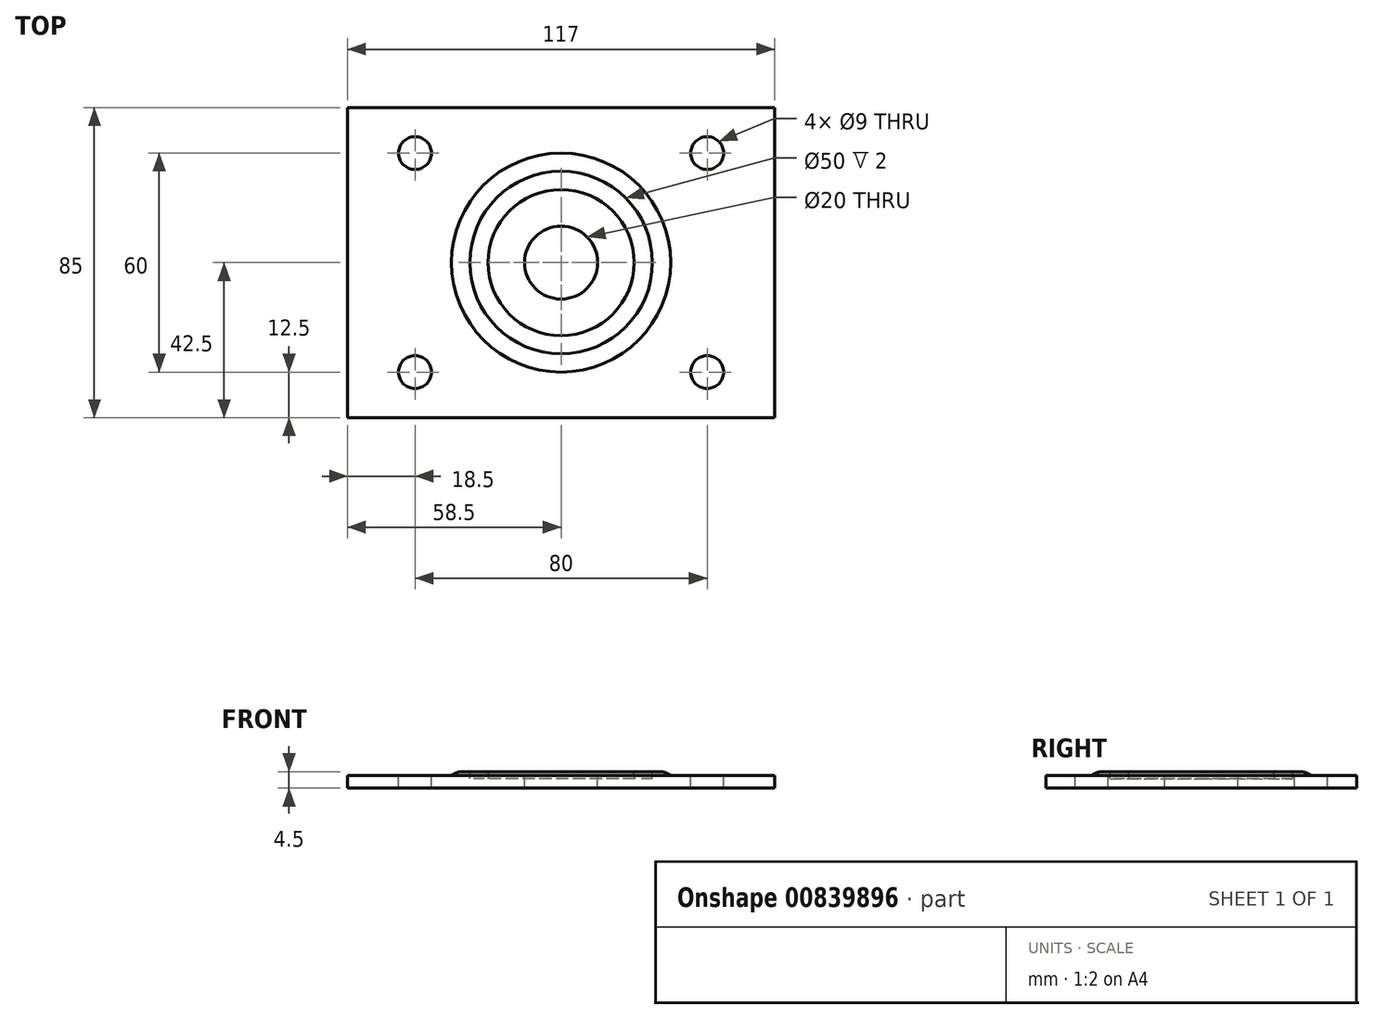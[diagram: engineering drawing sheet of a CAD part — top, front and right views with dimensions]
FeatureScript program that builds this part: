
annotation { "Feature Type Name" : "Feature", "Feature Type Description" : "" }
export const myFeature = defineFeature(function(context is Context, id is Id, definition is map)
    precondition{}
    {
        {
            var Q0;
            Q0=qCreatedBy(makeId("Top.planeOp"),FACE);
            var sketch = newSketch(context, id + "F0", { "sketchPlane" : qUnion([Q0])});
            skLineSegment(sketch, "E0.bottom", {"start": v(58.5, -42.5) * mm, "end": v(-58.5, -42.5) * mm});
            skLineSegment(sketch, "E0.top", {"start": v(58.5, 42.5) * mm, "end": v(-58.5, 42.5) * mm});
            skLineSegment(sketch, "E0.left", {"start": v(58.5, -42.5) * mm, "end": v(58.5, 42.5) * mm});
            skLineSegment(sketch, "E0.right", {"start": v(-58.5, -42.5) * mm, "end": v(-58.5, 42.5) * mm});
            skPoint(sketch, "E0.middle", {"position": v(0, 0) * mm});
            skSolve(sketch);
        }
        {
            var Q0;
            Q0 = qSketchRegion(id + "F0", true);
            extrude(context, id + "F1", {"entities" : qUnion([Q0]), "depth" : 3.5 * mm, "offsetDistance" : 25 * mm});
        }
        {
            var Q0;
            Q0=makeQuery(id+"F1.opExtrude","CAP_FACE",FACE,{"disambiguationData":[OSD([sQuery(id+"F0.wireOp",EDGE,"E0.bottom"),sQuery(id+"F0.wireOp",EDGE,"E0.top"),sQuery(id+"F0.wireOp",EDGE,"E0.left"),sQuery(id+"F0.wireOp",EDGE,"E0.right")])],"isStart":false});
            var sketch = newSketch(context, id + "F2", { "sketchPlane" : qUnion([Q0])});
            skLineSegment(sketch, "E1.bottom", {"start": v(40, -30) * mm, "end": v(-40, -30) * mm, "construction": true});
            skLineSegment(sketch, "E1.top", {"start": v(40, 30) * mm, "end": v(-40, 30) * mm, "construction": true});
            skLineSegment(sketch, "E1.left", {"start": v(40, -30) * mm, "end": v(40, 30) * mm, "construction": true});
            skLineSegment(sketch, "E1.right", {"start": v(-40, -30) * mm, "end": v(-40, 30) * mm, "construction": true});
            skPoint(sketch, "E1.middle", {"position": v(0, 0) * mm});
            skCircle(sketch, "E2", {"center": v(40, 30) * mm, "radius": 4.5 * mm});
            skCircle(sketch, "E3", {"center": v(-40, 30) * mm, "radius": 4.5 * mm});
            skCircle(sketch, "E4", {"center": v(-40, -30) * mm, "radius": 4.5 * mm});
            skCircle(sketch, "E5", {"center": v(40, -30) * mm, "radius": 4.5 * mm});
            skSolve(sketch);
        }
        {
            var Q0;
            Q0 = qSketchRegion(id + "F2", true);
            extrude(context, id + "F3", {"entities" : qUnion([Q0]), "operationType" : NewBodyOperationType.REMOVE, "oppositeDirection" : true, "depth" : 25 * mm, "offsetDistance" : 25 * mm});
        }
        {
            var Q0;
            Q0=makeQuery(id+"F1.opExtrude","CAP_FACE",FACE,{"disambiguationData":[OSD([sQuery(id+"F0.wireOp",EDGE,"E0.bottom"),sQuery(id+"F0.wireOp",EDGE,"E0.top"),sQuery(id+"F0.wireOp",EDGE,"E0.left"),sQuery(id+"F0.wireOp",EDGE,"E0.right")])],"isStart":false});
            var sketch = newSketch(context, id + "F4", { "sketchPlane" : qUnion([Q0])});
            skCircle(sketch, "E6", {"center": v(0, 0) * mm, "radius": 30 * mm});
            skSolve(sketch);
        }
        {
            var Q0;
            Q0 = qSketchRegion(id + "F4", true);
            extrude(context, id + "F5", {"entities" : qUnion([Q0]), "operationType" : NewBodyOperationType.ADD, "depth" : 1 * mm, "offsetDistance" : 25 * mm});
        }
        {
            var Q0;
            Q0=makeQuery(id+"F5.opExtrude","CAP_EDGE",EDGE,{"disambiguationData":[OSD([sQuery(id+"F4.wireOp",EDGE,"E6")])],"isStart":false});
            fillet(context, id + "F6", {"entities" : qUnion([Q0]), "radius" : 5 * mm, "tangentPropagation" : true, "allowEdgeOverflow" : false});
        }
        {
            var Q0;
            Q0=makeQuery(id+"F5.opExtrude","CAP_FACE",FACE,{"disambiguationData":[OSD([sQuery(id+"F4.wireOp",EDGE,"E6")])],"isStart":false});
            var sketch = newSketch(context, id + "F7", { "sketchPlane" : qUnion([Q0])});
            skCircle(sketch, "E7", {"center": v(0, 0) * mm, "radius": 25 * mm});
            skSolve(sketch);
        }
        {
            var Q0;
            Q0 = qSketchRegion(id + "F7", true);
            extrude(context, id + "F8", {"entities" : qUnion([Q0]), "operationType" : NewBodyOperationType.REMOVE, "oppositeDirection" : true, "depth" : 2 * mm, "offsetDistance" : 25 * mm});
        }
        {
            var Q0;
            Q0=makeQuery(id+"F8.boolean.opBoolean","COPY",FACE,{"derivedFrom":makeQuery(id+"F8.opExtrude","CAP_FACE",FACE,{"disambiguationData":[OSD([sQuery(id+"F7.wireOp",EDGE,"E7")])],"isStart":false})});
            var sketch = newSketch(context, id + "F9", { "sketchPlane" : qUnion([Q0])});
            skCircle(sketch, "E8", {"center": v(0, 0) * mm, "radius": 20 * mm});
            skSolve(sketch);
        }
        {
            var Q0;
            Q0 = qSketchRegion(id + "F9", true);
            extrude(context, id + "F10", {"entities" : qUnion([Q0]), "operationType" : NewBodyOperationType.ADD, "depth" : 2 * mm, "offsetDistance" : 25 * mm});
        }
        {
            var Q0;
            Q0=makeQuery(id+"F10.opExtrude","CAP_EDGE",EDGE,{"disambiguationData":[OSD([sQuery(id+"F9.wireOp",EDGE,"E8")])],"isStart":false});
            fillet(context, id + "F11", {"entities" : qUnion([Q0]), "radius" : 1 * mm, "tangentPropagation" : true, "allowEdgeOverflow" : false});
        }
        {
            var Q0;
            Q0=makeQuery(id+"F10.opExtrude","CAP_FACE",FACE,{"disambiguationData":[OSD([sQuery(id+"F9.wireOp",EDGE,"E8")])],"isStart":false});
            var sketch = newSketch(context, id + "F12", { "sketchPlane" : qUnion([Q0])});
            skCircle(sketch, "E9", {"center": v(0, 0) * mm, "radius": 10 * mm});
            skSolve(sketch);
        }
        {
            var Q0;
            Q0 = qSketchRegion(id + "F12", true);
            extrude(context, id + "F13", {"entities" : qUnion([Q0]), "operationType" : NewBodyOperationType.REMOVE, "oppositeDirection" : true, "depth" : 25 * mm, "offsetDistance" : 25 * mm});
        }
    });
